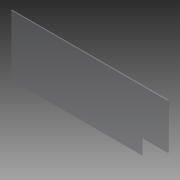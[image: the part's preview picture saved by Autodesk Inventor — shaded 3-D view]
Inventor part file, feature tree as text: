
AUTODESK INVENTOR PART (.ipt)
format: ipt  version: 2014 (Build 180170000, 170)  size: 78,848 bytes
history: native  units: in
note: dims shown in document units (in); Inventor stores cm internally (conversion verified against a paired STEP export)
features: extrude x1
ambient origin geometry x8: Origin, YZ Plane, XZ Plane, XY Plane, X Axis, Y Axis, Z Axis, Center Point
bodies: Solid1 (feature_tree)
feature tree (1):
  extrude  "Extrusion1"  Depth=20.8in
